# Revit family: R 502 G
name_source: partatom
category: Equipement spécialisé
revit_build: Autodesk Revit LT 2017 (Build: 20160225_1515(x64)
units: mm (PartAtom-declared; Revit-internal decimal feet)

## family parameters
Basée sur le plan de construction = Non
Cote de connecteur circulaire = Utiliser le rayon
Couper avec des vides une fois chargée = Non
Numéro OmniClass = 23.40.40.14.14.11
Partagée = Non
Point de calcul de pièce = Non
Titre OmniClass = Food Mixers
Toujours verticalement = Oui
Type d'élément = Normal

## types (3) — shared parameters
Apparent Power = 0 VA
Depth Coupe-Légumes = 590 mm
Depth Cutter = 348 mm  [stored 1.14173 ft]
Description = COMBINES
Fabricant = ROBOT COUPE
Height Coupe-Légumes = 672 mm
Height Cutter = 539 mm
Modèle = R 502 G
Phase = 3
UP Depth Coupe-Légumes = 636 mm
UP Height Coupe-Légumes = 820 mm
UP Width Coupe-Légumes = 599 mm
URL = www.robot-coupe.com
Watts = 900 W
Weight = 30 kg
Width Coupe-Légumes = 475 mm
Width Cutter = 278 mm
Width Electrique connexion Coupe-Légumes = 272 mm
Width Electrique connexion Cutter = 173 mm
water = Connector
zero-valued in all types: Cold water supply, Cold water supply height, Used water, Waste water height

## per-type parameters (varying)
| type | Amps | Cycle | Speeds (Rpm) | Volts |
| R 502 G    400/50/3 | 2.2 A | 50 Hz | 750 and 1500 | 400 V |
| R 502 G    220/60/3 | 3.8 A | 60 Hz | 900 and 1800 | 220 V |
| R 502 G    230/50/3 | 2.4 A | 50 Hz | 750 and 1500 | 230 V |

note: [stored X ft] marks values corroborated as IEEE doubles in the binary element streams (Revit-internal decimal feet)

## geometry (parser evidence)
native form markers: Sweep x3
no freeform markers — native parametric forms only
